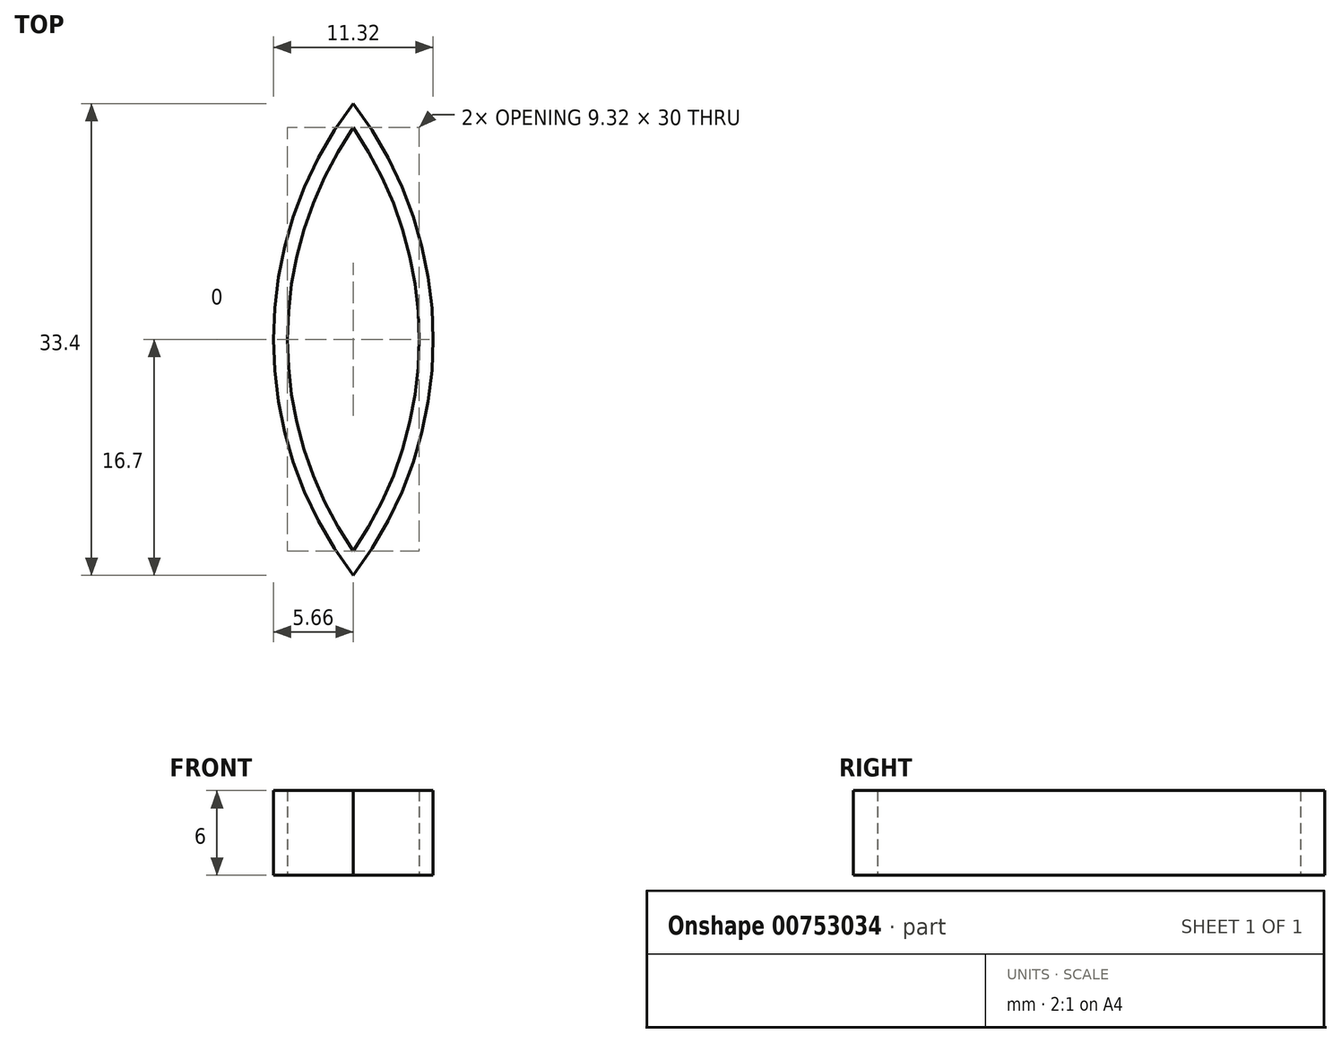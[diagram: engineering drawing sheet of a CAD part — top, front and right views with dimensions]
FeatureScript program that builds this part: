
annotation { "Feature Type Name" : "Feature", "Feature Type Description" : "" }
export const myFeature = defineFeature(function(context is Context, id is Id, definition is map)
    precondition{}
    {
        {
            var Q0;
            Q0=qCreatedBy(makeId("Top.planeOp"),FACE);
            var sketch = newSketch(context, id + "F0", { "sketchPlane" : qUnion([Q0])});
            skArc(sketch, "E0", {"start": v(0, -15) * mm, "mid": v(4.66, 0) * mm, "end": v(0, 15) * mm});
            skArc(sketch, "E1", {"start": v(0, 15) * mm, "mid": v(-4.66, 0) * mm, "end": v(0, -15) * mm});
            skLineSegment(sketch, "E2", {"start": v(0, 15) * mm, "end": v(0, -15) * mm, "construction": true});
            skArc(sketch, "E3.0", {"start": v(0, 16.7) * mm, "mid": v(-5.66, 0) * mm, "end": v(0, -16.7) * mm});
            skArc(sketch, "E3.1", {"start": v(0, -16.7) * mm, "mid": v(5.66, 0) * mm, "end": v(0, 16.7) * mm});
            skSolve(sketch);
        }
        {
            var Q0;
            Q0=qSketchRegion(id+"F0",true);
            extrude(context, id + "F1", {"entities" : qUnion([Q0]), "depth" : 6 * mm, "offsetDistance" : 25 * mm});
        }
    });
